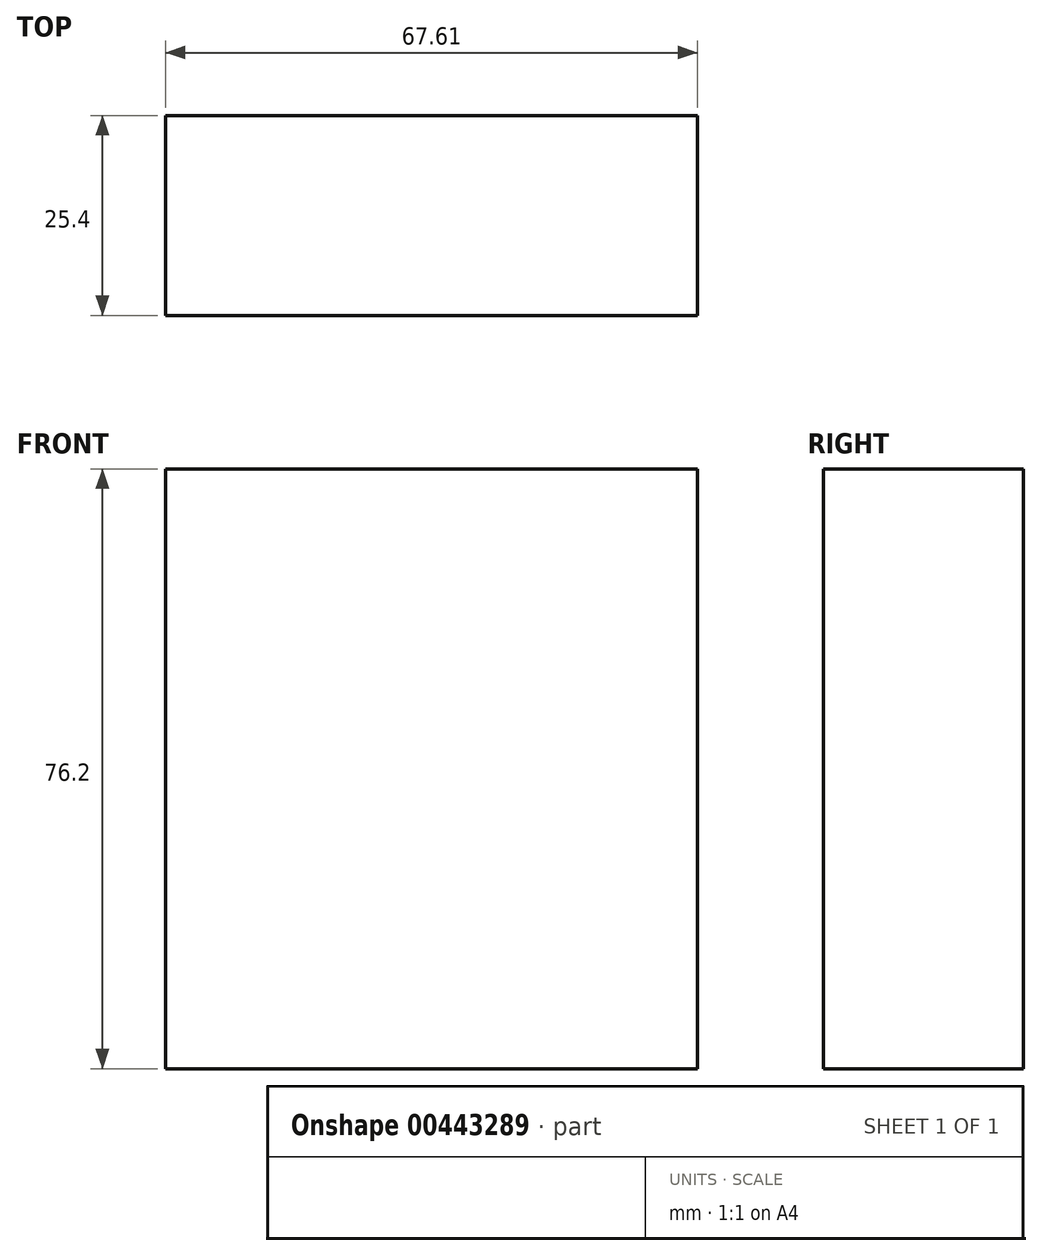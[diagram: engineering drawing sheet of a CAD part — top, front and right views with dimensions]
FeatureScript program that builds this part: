
annotation { "Feature Type Name" : "Feature", "Feature Type Description" : "" }
export const myFeature = defineFeature(function(context is Context, id is Id, definition is map)
    precondition{}
    {
        {
            var Q0;
            Q0=qCreatedBy(makeId("Front.planeOp"),FACE);
            var sketch = newSketch(context, id + "F0", { "sketchPlane" : qUnion([Q0])});
            skLineSegment(sketch, "E0.bottom", {"start": v(-31.92, 42.8) * mm, "end": v(35.7, 42.8) * mm});
            skLineSegment(sketch, "E0.top", {"start": v(-31.92, -33.4) * mm, "end": v(35.7, -33.4) * mm});
            skLineSegment(sketch, "E0.left", {"start": v(-31.92, 42.8) * mm, "end": v(-31.92, -33.4) * mm});
            skLineSegment(sketch, "E0.right", {"start": v(35.7, 42.8) * mm, "end": v(35.7, -33.4) * mm});
            skSolve(sketch);
        }
        {
            var Q0;
            Q0 = qSketchRegion(id + "F0", true);
            extrude(context, id + "F1", {"entities" : qUnion([Q0]), "depth" : 25.4 * mm});
        }
    });
